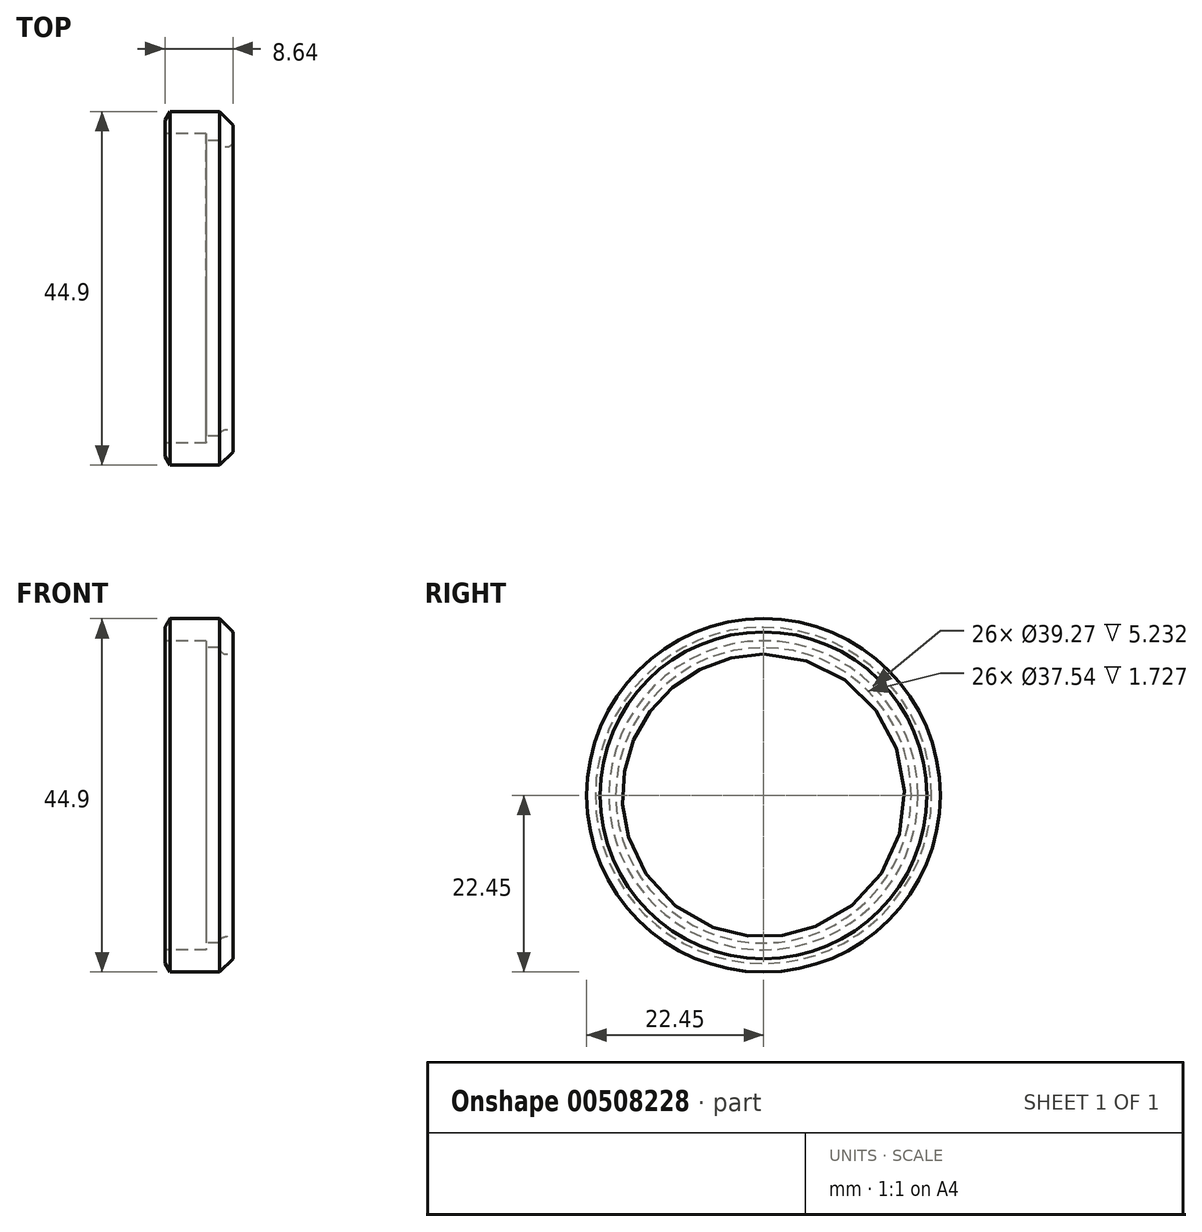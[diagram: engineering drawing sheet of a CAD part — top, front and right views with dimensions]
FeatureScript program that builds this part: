
annotation { "Feature Type Name" : "Feature", "Feature Type Description" : "" }
export const myFeature = defineFeature(function(context is Context, id is Id, definition is map)
    precondition{}
    {
        {
            var Q0;
            Q0=qCreatedBy(makeId("Front.planeOp"),FACE);
            var sketch = newSketch(context, id + "F0", { "sketchPlane" : qUnion([Q0])});
            skLineSegment(sketch, "E0", {"start": v(-4.95, 0) * mm, "end": v(5.09, 0) * mm});
            skLineSegment(sketch, "E1", {"start": v(-3.54, 19.63) * mm, "end": v(1.7, 19.63) * mm});
            skLineSegment(sketch, "E2", {"start": v(1.7, 19.63) * mm, "end": v(1.7, 18.77) * mm});
            skLineSegment(sketch, "E3", {"start": v(1.7, 18.77) * mm, "end": v(3.42, 18.77) * mm});
            skLineSegment(sketch, "E4", {"start": v(5.1, 18.77) * mm, "end": v(5.1, 20.76) * mm});
            skLineSegment(sketch, "E5", {"start": v(5.1, 20.76) * mm, "end": v(3.42, 22.45) * mm});
            skLineSegment(sketch, "E6", {"start": v(3.42, 22.45) * mm, "end": v(-2.9, 22.45) * mm});
            skLineSegment(sketch, "E7", {"start": v(-2.9, 22.45) * mm, "end": v(-3.54, 21.35) * mm});
            skLineSegment(sketch, "E8", {"start": v(-3.54, 21.35) * mm, "end": v(-3.54, 19.63) * mm});
            skArc(sketch, "E9", {"start": v(3.42, 18.77) * mm, "mid": v(4.26, 17.93) * mm, "end": v(5.1, 18.77) * mm});
            skSolve(sketch);
        }
        {
            var Q0;
            Q0=makeQuery(id+"F0.imprint","IMPRINT",FACE,{"disambiguationData":[TD([[makeQuery(id+"F0.imprint","IMPRINT",EDGE,{"derivedFrom":sQuery(id+"F0.wireOp",EDGE,"E1")}),1.0]])]});
            var Q1;
            Q1=sQuery(id+"F0.wireOp",EDGE,"E0");
            revolve(context, id + "F1", {"entities" : qUnion([Q0]), "axis" : qUnion([Q1]), "revolveType" : RevolveType.FULL});
        }
    });
